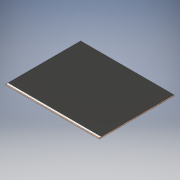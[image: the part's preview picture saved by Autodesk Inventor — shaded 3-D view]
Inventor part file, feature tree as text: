
AUTODESK INVENTOR PART (.ipt)
format: ipt  version: 2017 (Build 210142000, 142)  size: 102,400 bytes
history: native  units: in
note: dims shown in document units (in); Inventor stores cm internally (conversion verified against a paired STEP export)
features: extrude x2, sketch x2
ambient origin geometry x8: Origin, YZ Plane, XZ Plane, XY Plane, X Axis, Y Axis, Z Axis, Center Point
bodies: Solid1 (feature_tree)
feature tree (4):
  extrude  "Extrusion1"  Depth=36.0in
  extrude  "Extrusion2"  Depth=1.0in
  sketch  "Sketch1"  dims[d0=45.0in d1=36.0in]
  sketch  "Sketch2"  dims[d2=0.5in d3=0.0in d4=1.0in d5=0.001in d6=0.0in]
